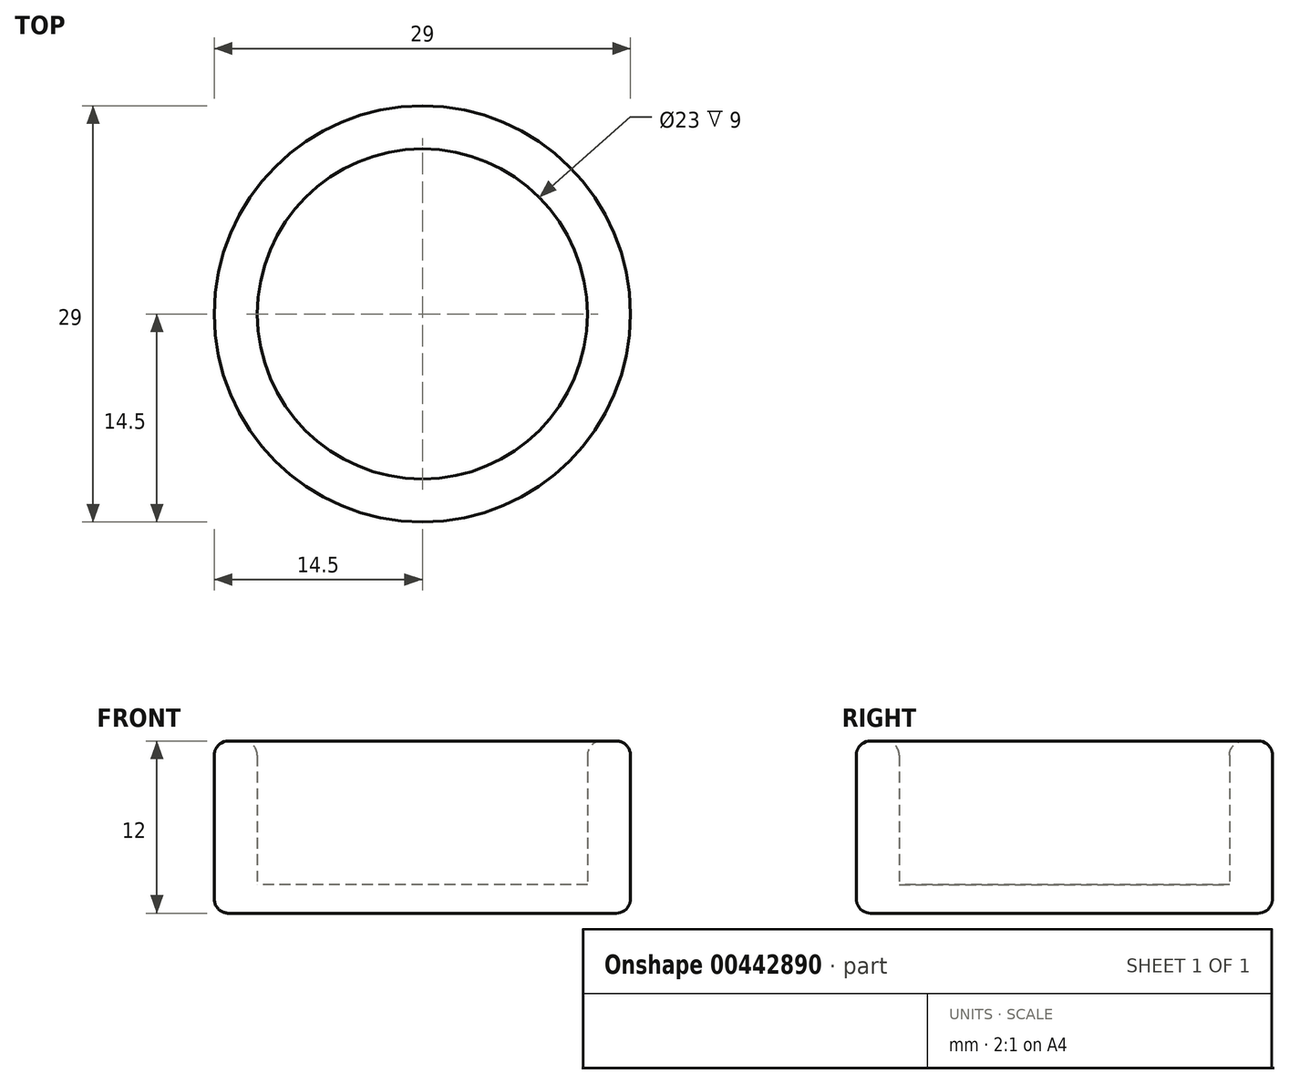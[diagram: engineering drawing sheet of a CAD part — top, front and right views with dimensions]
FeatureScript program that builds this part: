
annotation { "Feature Type Name" : "Feature", "Feature Type Description" : "" }
export const myFeature = defineFeature(function(context is Context, id is Id, definition is map)
    precondition{}
    {
        {
            var Q0;
            Q0=qCreatedBy(makeId("Top.planeOp"),FACE);
            var sketch = newSketch(context, id + "F0", { "sketchPlane" : qUnion([Q0])});
            skCircle(sketch, "E0", {"center": v(0, 0) * mm, "radius": 14.5 * mm});
            skCircle(sketch, "E1", {"center": v(0, 0) * mm, "radius": 11.5 * mm});
            skSolve(sketch);
        }
        {
            var Q0;
            Q0=makeQuery(id+"F0.imprint","IMPRINT",FACE,{"disambiguationData":[TD([[makeQuery(id+"F0.imprint","IMPRINT",EDGE,{"derivedFrom":sQuery(id+"F0.wireOp",EDGE,"E0")}),1.0]])]});
            extrude(context, id + "F1", {"entities" : qUnion([Q0]), "depth" : 10 * mm});
        }
        {
            var Q0;
            Q0=makeQuery(id+"F1.opExtrude","CAP_FACE",FACE,{"disambiguationData":[OSD([sQuery(id+"F0.wireOp",EDGE,"E0"),sQuery(id+"F0.wireOp",EDGE,"E1")])],"isStart":true});
            var sketch = newSketch(context, id + "F2", { "sketchPlane" : qUnion([Q0])});
            skCircle(sketch, "E2", {"center": v(0, 0) * mm, "radius": 14.5 * mm});
            skSolve(sketch);
        }
        {
            var Q0;
            Q0 = qSketchRegion(id + "F2", true);
            extrude(context, id + "F3", {"entities" : qUnion([Q0]), "operationType" : NewBodyOperationType.ADD, "depth" : 2 * mm});
        }
        {
            var Q0;
            Q0=makeQuery(id+"F1.opExtrude","CAP_EDGE",EDGE,{"disambiguationData":[OSD([sQuery(id+"F0.wireOp",EDGE,"E0")])],"isStart":false});
            var Q1;
            Q1=makeQuery(id+"F1.opExtrude","CAP_EDGE",EDGE,{"disambiguationData":[OSD([sQuery(id+"F0.wireOp",EDGE,"E1")])],"isStart":false});
            var Q2;
            Q2=makeQuery(id+"F3.opExtrude","CAP_EDGE",EDGE,{"disambiguationData":[OSD([sQuery(id+"F2.wireOp",EDGE,"E2")])],"isStart":false});
            fillet(context, id + "F4", {"entities" : qUnion([Q0, Q1, Q2]), "radius" : 1 * mm, "tangentPropagation" : true, "allowEdgeOverflow" : false});
        }
    });
